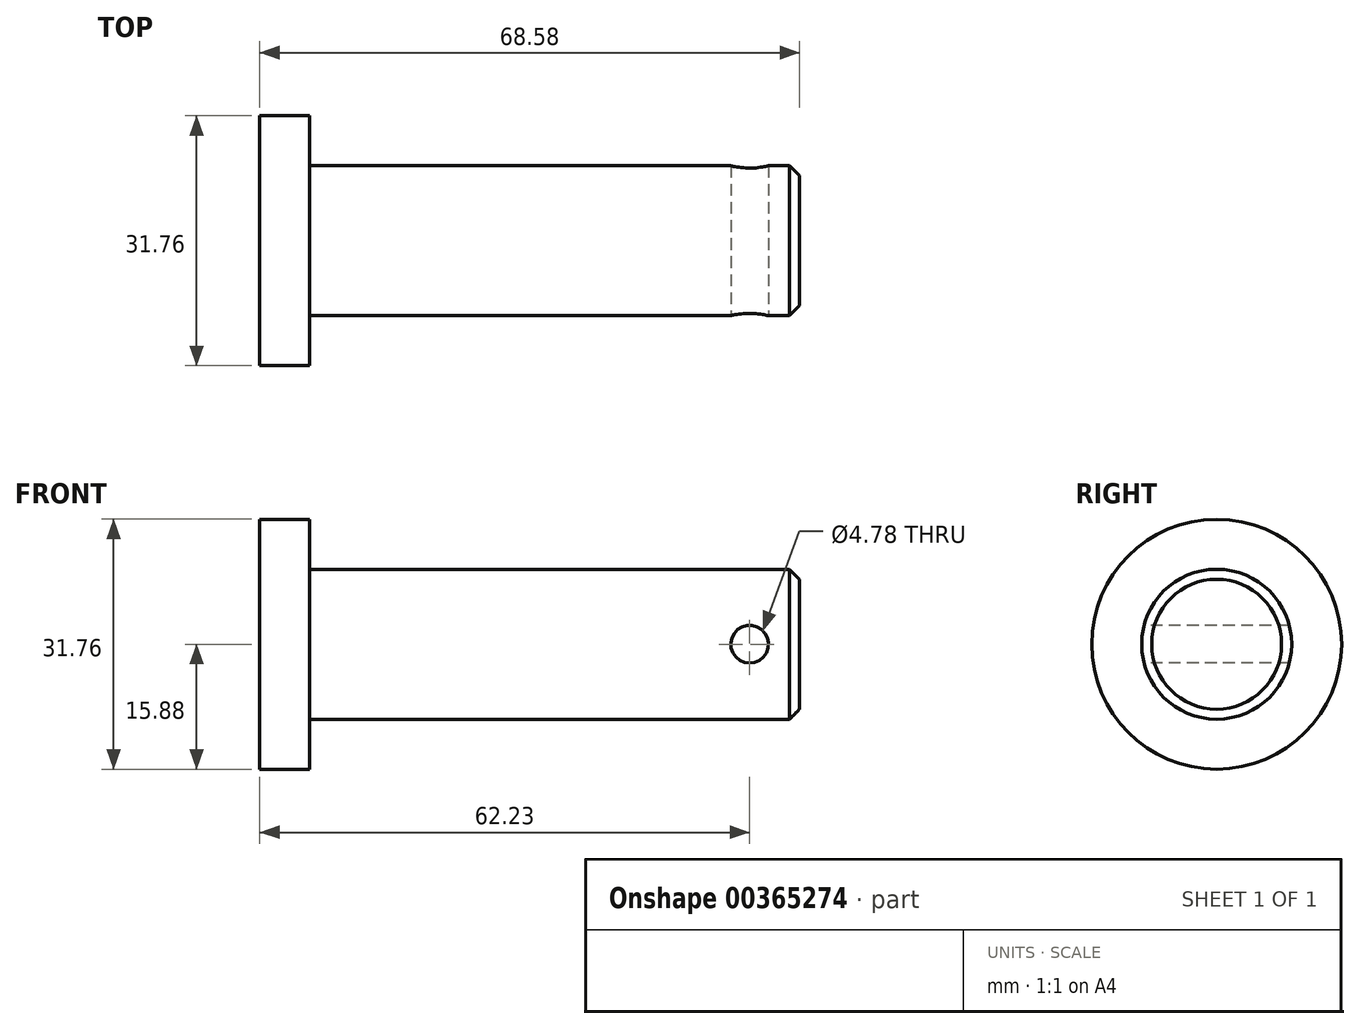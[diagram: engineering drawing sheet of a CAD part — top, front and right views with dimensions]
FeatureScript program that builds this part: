
annotation { "Feature Type Name" : "Feature", "Feature Type Description" : "" }
export const myFeature = defineFeature(function(context is Context, id is Id, definition is map)
    precondition{}
    {
        {
            var Q0;
            Q0=qCreatedBy(makeId("Right.planeOp"),FACE);
            var sketch = newSketch(context, id + "F0", { "sketchPlane" : qUnion([Q0])});
            skCircle(sketch, "E0", {"center": v(0, 0) * mm, "radius": 15.88 * mm});
            skCircle(sketch, "E1", {"center": v(0, 0) * mm, "radius": 9.53 * mm});
            skSolve(sketch);
        }
        {
            var Q0;
            Q0 = qSketchRegion(id + "F0", true);
            var Q1;
            Q1=makeQuery(id+"F0.imprint","IMPRINT",FACE,{"disambiguationData":[TD([[makeQuery(id+"F0.imprint","IMPRINT",EDGE,{"derivedFrom":sQuery(id+"F0.wireOp",EDGE,"E1")}),1.0]])]});
            extrude(context, id + "F1", {"entities" : qUnion([Q0, Q1]), "oppositeDirection" : true, "depth" : 6.35 * mm});
        }
        {
            var Q0;
            Q0=makeQuery(id+"F0.imprint","IMPRINT",FACE,{"disambiguationData":[TD([[makeQuery(id+"F0.imprint","IMPRINT",EDGE,{"derivedFrom":sQuery(id+"F0.wireOp",EDGE,"E1")}),1.0]])]});
            extrude(context, id + "F2", {"entities" : qUnion([Q0]), "operationType" : NewBodyOperationType.ADD, "depth" : 62.23 * mm});
        }
        {
            var Q0;
            Q0=qCreatedBy(makeId("Front.planeOp"),FACE);
            var sketch = newSketch(context, id + "F3", { "sketchPlane" : qUnion([Q0])});
            skCircle(sketch, "E2", {"center": v(55.88, 0) * mm, "radius": 2.39 * mm});
            skSolve(sketch);
        }
        {
            var Q0;
            Q0 = qSketchRegion(id + "F3", true);
            extrude(context, id + "F4", {"entities" : qUnion([Q0]), "operationType" : NewBodyOperationType.REMOVE, "endBound" : BoundingType.THROUGH_ALL, "oppositeDirection" : true, "depth" : 25.4 * mm, "hasSecondDirection" : true, "secondDirectionOppositeDirection" : false, "secondDirectionDepth" : 25.4 * mm});
        }
        {
            var Q0;
            Q0=makeQuery(id+"F2.opExtrude","CAP_EDGE",EDGE,{"disambiguationData":[OSD([sQuery(id+"F0.wireOp",EDGE,"E1")])],"isStart":false});
            chamfer(context, id + "F5", {"entities" : qUnion([Q0]), "chamferType" : ChamferType.OFFSET_ANGLE, "width" : 1.27 * mm, "oppositeDirection" : false, "angle" : 45 * degree, "tangentPropagation" : true});
        }
    });
